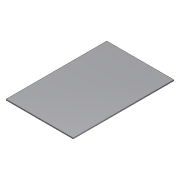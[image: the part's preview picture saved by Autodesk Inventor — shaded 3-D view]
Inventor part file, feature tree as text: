
AUTODESK INVENTOR PART (.ipt)
format: ipt  version: 2012 (Build 160160000, 160)  size: 67,072 bytes
history: native  units: in
note: dims shown in document units (in); Inventor stores cm internally (conversion verified against a paired STEP export)
features: extrude x1, sketch x1
ambient origin geometry x8: Origin, YZ Plane, XZ Plane, XY Plane, X Axis, Y Axis, Z Axis, Center Point
bodies: Solid1 (feature_tree)
feature tree (2):
  extrude  "Extrusion1"  Depth=72.0in
  sketch  "Sketch2"  dims[d0=108.0in d1=72.0in d2=1.0in d3=0.0in]
